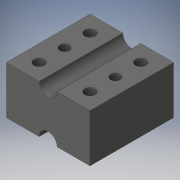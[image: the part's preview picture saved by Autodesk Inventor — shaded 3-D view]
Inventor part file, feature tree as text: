
AUTODESK INVENTOR PART (.ipt)
format: ipt  version: 2016 SP1 (Build 200210100, 210)  size: 136,704 bytes
history: native  units: in
note: dims shown in document units (in); Inventor stores cm internally (conversion verified against a paired STEP export)
features: sketch x4, extrude x2, hole x2
ambient origin geometry x8: Origin, YZ Plane, XZ Plane, XY Plane, X Axis, Y Axis, Z Axis, Center Point
bodies: Solid1 (feature_tree)
feature tree (8):
  extrude  "Extrusion1"  Depth=1.75in
  hole  "Hole1"  [1 undecoded]
  hole  "Hole2"  [1 undecoded]
  extrude  "Extrusion2"  TaperAngle=0.0deg  [1 undecoded]
  sketch  "Sketch1"  dims[d0=1.75in d1=0.4375in]
  sketch  "Sketch3"  dims[d2=0.0in d3=0.375in]
  sketch  "Sketch4"  dims[d5=0.0in d4=1.75in]
  sketch  "Sketch5"  dims[d6=1.0in d7=0.0in d9=0.375in d10=0.75in d11=0.375in d12=0.25in d13=0.5635in d14=1.0in d15=0.8108in d16=0.3438in d17=0.3438in d18=0.201in d19=0.75in d20=0.385in d21=0.25in d22=0.5635in d23=1.0in d24=0.8108in d25=0.875in d26=0.875in d27=0.3438in d28=0.3438in d29=0.22in d30=0.0in d31=0.0in]
note: 3 required parameter values undecoded (feature->parameter linkage not recoverable at this tier; creation-order binding heuristic only, values carry confidence <= 0.55)
